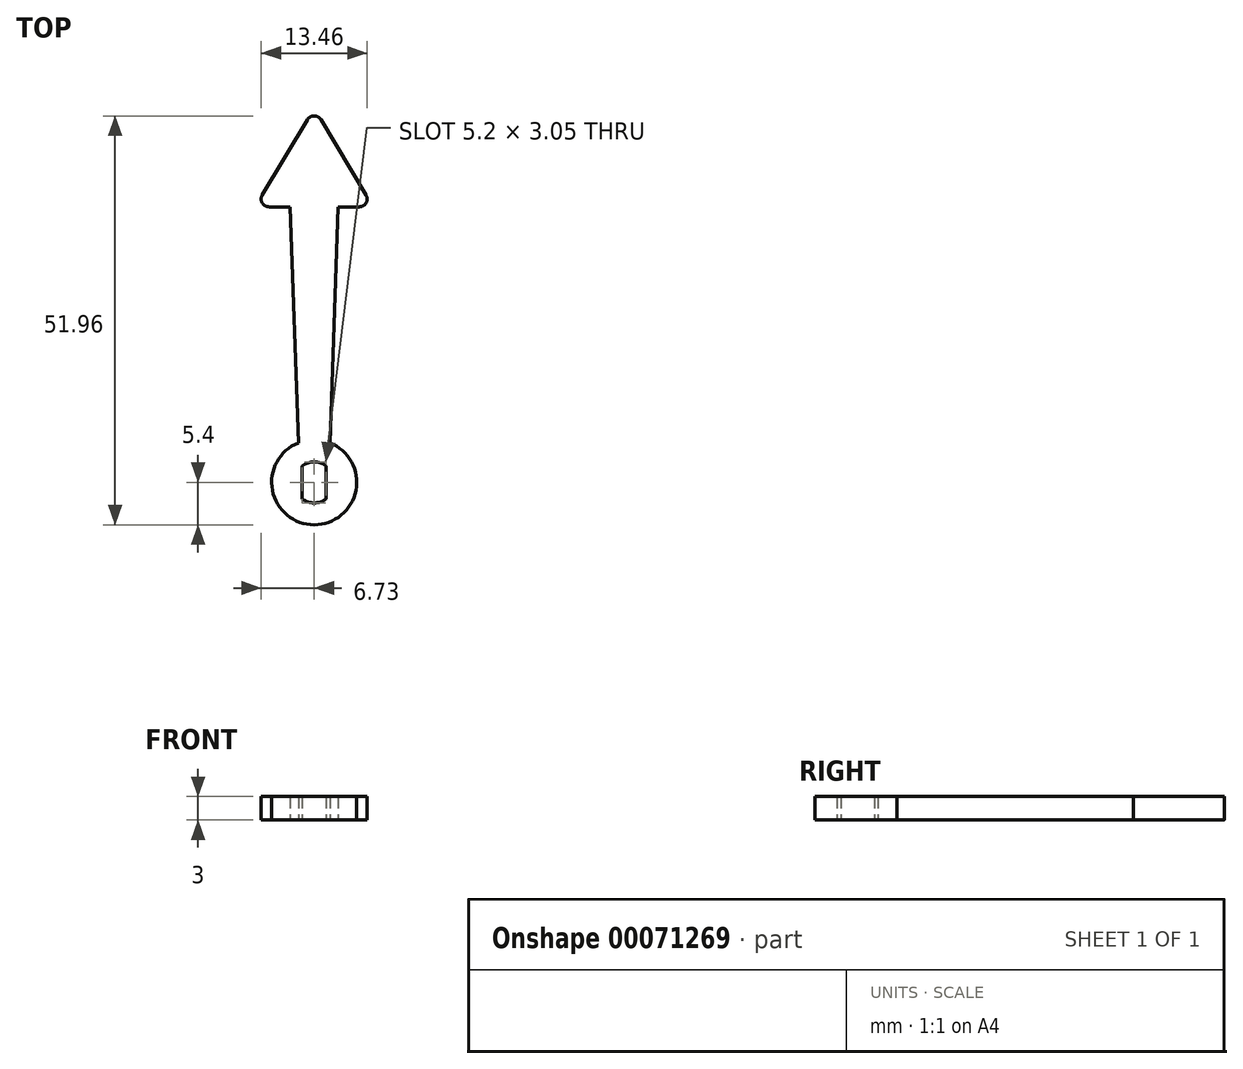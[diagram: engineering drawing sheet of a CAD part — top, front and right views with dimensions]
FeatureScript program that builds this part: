
annotation { "Feature Type Name" : "Feature", "Feature Type Description" : "" }
export const myFeature = defineFeature(function(context is Context, id is Id, definition is map)
    precondition{}
    {
        {
            var Q0;
            Q0=qCreatedBy(makeId("Top.planeOp"),FACE);
            var sketch = newSketch(context, id + "F0", { "sketchPlane" : qUnion([Q0])});
            skCircle(sketch, "E0", {"center": v(0, 0) * mm, "radius": 5.4 * mm});
            skCircle(sketch, "E1", {"center": v(0, 0) * mm, "radius": 2.6 * mm});
            skLineSegment(sketch, "E2", {"start": v(-1.53, 2.1) * mm, "end": v(-1.52, -2.1) * mm});
            skLineSegment(sketch, "E3", {"start": v(1.52, 2.1) * mm, "end": v(1.53, -2.1) * mm});
            skSolve(sketch);
        }
        {
            var Q0;
            {var subQ0=sQuery(id+"F0.wireOp",EDGE,"E2");Q0=makeQuery(id+"F0.imprint","IMPRINT",FACE,{"disambiguationData":[TD([[makeQuery(id+"F0.imprint","IMPRINT",EDGE,{"derivedFrom":subQ0}),-1.0]])]});}
            var Q1;
            Q1=makeQuery(id+"F0.imprint","IMPRINT",FACE,{"disambiguationData":[TD([[makeQuery(id+"F0.imprint","IMPRINT",EDGE,{"derivedFrom":sQuery(id+"F0.wireOp",EDGE,"E0")}),1.0]])]});
            var Q2;
            {var subQ0=sQuery(id+"F0.wireOp",EDGE,"E3");Q2=makeQuery(id+"F0.imprint","IMPRINT",FACE,{"disambiguationData":[TD([[makeQuery(id+"F0.imprint","IMPRINT",EDGE,{"derivedFrom":subQ0}),1.0]])]});}
            extrude(context, id + "F1", {"entities" : qUnion([Q0, Q1, Q2]), "depth" : 3 * mm});
        }
        {
            var Q0;
            Q0=qCreatedBy(makeId("Top.planeOp"),FACE);
            var sketch = newSketch(context, id + "F2", { "sketchPlane" : qUnion([Q0])});
            skLineSegment(sketch, "E4", {"start": v(0, 0) * mm, "end": v(0, 35) * mm, "construction": true});
            skLineSegment(sketch, "E5", {"start": v(0, 5.02) * mm, "end": v(2, 5.02) * mm});
            skLineSegment(sketch, "E6", {"start": v(0, 35) * mm, "end": v(3.05, 35) * mm});
            skLineSegment(sketch, "E7", {"start": v(3.05, 35) * mm, "end": v(2, 5.02) * mm});
            skLineSegment(sketch, "E8.MirrorCS", {"start": v(0, 5.02) * mm, "end": v(-2, 5.02) * mm});
            skLineSegment(sketch, "E9.MirrorCS", {"start": v(0, 35) * mm, "end": v(-3.05, 35) * mm});
            skLineSegment(sketch, "E10.MirrorCS", {"start": v(-3.05, 35) * mm, "end": v(-2, 5.02) * mm});
            skSolve(sketch);
        }
        {
            var Q0;
            Q0 = qSketchRegion(id + "F2", true);
            var Q1;
            Q1=makeQuery(id+"F1.opExtrude","CAP_FACE",FACE,{"disambiguationData":[OSD([sQuery(id+"F0.wireOp",EDGE,"E0"),sQuery(id+"F0.wireOp",EDGE,"E1"),sQuery(id+"F0.wireOp",EDGE,"E2"),sQuery(id+"F0.wireOp",EDGE,"E3")])],"isStart":false});
            extrude(context, id + "F3", {"entities" : qUnion([Q0]), "operationType" : NewBodyOperationType.ADD, "endBound" : BoundingType.UP_TO_SURFACE, "endBoundEntityFace" : qUnion([Q1]), "depth" : 3 * mm});
        }
        {
            var Q0;
            Q0=qCreatedBy(makeId("Top.planeOp"),FACE);
            var sketch = newSketch(context, id + "F4", { "sketchPlane" : qUnion([Q0])});
            skLineSegment(sketch, "E11", {"start": v(0, 35) * mm, "end": v(0, 47.5) * mm, "construction": true});
            skLineSegment(sketch, "E12", {"start": v(-7.5, 35) * mm, "end": v(7.5, 35) * mm});
            skLineSegment(sketch, "E13", {"start": v(0, 47.5) * mm, "end": v(-7.5, 35) * mm});
            skLineSegment(sketch, "E14", {"start": v(0, 47.5) * mm, "end": v(7.5, 35) * mm});
            skSolve(sketch);
        }
        {
            var Q0;
            Q0=makeQuery(id+"F4.imprint","IMPRINT",FACE,{"disambiguationData":[TD([[makeQuery(id+"F4.imprint","IMPRINT",EDGE,{"derivedFrom":sQuery(id+"F4.wireOp",EDGE,"E12")}),1.0]])]});
            var Q1;
            Q1=makeQuery(id+"F3.boolean.opBoolean","MERGE",FACE,{"derivedFrom":[makeQuery(id+"F1.opExtrude","CAP_FACE",FACE,{"disambiguationData":[OSD([sQuery(id+"F0.wireOp",EDGE,"E0"),sQuery(id+"F0.wireOp",EDGE,"E1"),sQuery(id+"F0.wireOp",EDGE,"E2"),sQuery(id+"F0.wireOp",EDGE,"E3")])],"isStart":false}),makeQuery(id+"F3.opExtrude","CAP_FACE",FACE,{"disambiguationData":[OSD([sQuery(id+"F2.wireOp",EDGE,"E5"),sQuery(id+"F2.wireOp",EDGE,"E6"),sQuery(id+"F2.wireOp",EDGE,"E7"),sQuery(id+"F2.wireOp",EDGE,"E8.MirrorCS"),sQuery(id+"F2.wireOp",EDGE,"E9.MirrorCS"),sQuery(id+"F2.wireOp",EDGE,"E10.MirrorCS")])],"isStart":false})]});
            extrude(context, id + "F5", {"entities" : qUnion([Q0]), "operationType" : NewBodyOperationType.ADD, "endBound" : BoundingType.UP_TO_SURFACE, "endBoundEntityFace" : qUnion([Q1]), "depth" : 25 * mm});
        }
        {
            var Q0;
            Q0=makeQuery(id+"F5.opExtrude","SWEPT_EDGE",EDGE,{"disambiguationData":[OSD([sQuery(id+"F4.wireOp",EDGE,"E13"),sQuery(id+"F4.wireOp",EDGE,"E14")])]});
            var Q1;
            Q1=makeQuery(id+"F5.opExtrude","SWEPT_EDGE",EDGE,{"disambiguationData":[OSD([sQuery(id+"F4.wireOp",EDGE,"E12"),sQuery(id+"F4.wireOp",EDGE,"E13")])]});
            var Q2;
            Q2=makeQuery(id+"F5.opExtrude","SWEPT_EDGE",EDGE,{"disambiguationData":[OSD([sQuery(id+"F4.wireOp",EDGE,"E12"),sQuery(id+"F4.wireOp",EDGE,"E14")])]});
            fillet(context, id + "F6", {"entities" : qUnion([Q0, Q1, Q2]), "radius" : 1 * mm, "tangentPropagation" : true, "allowEdgeOverflow" : false});
        }
    });
